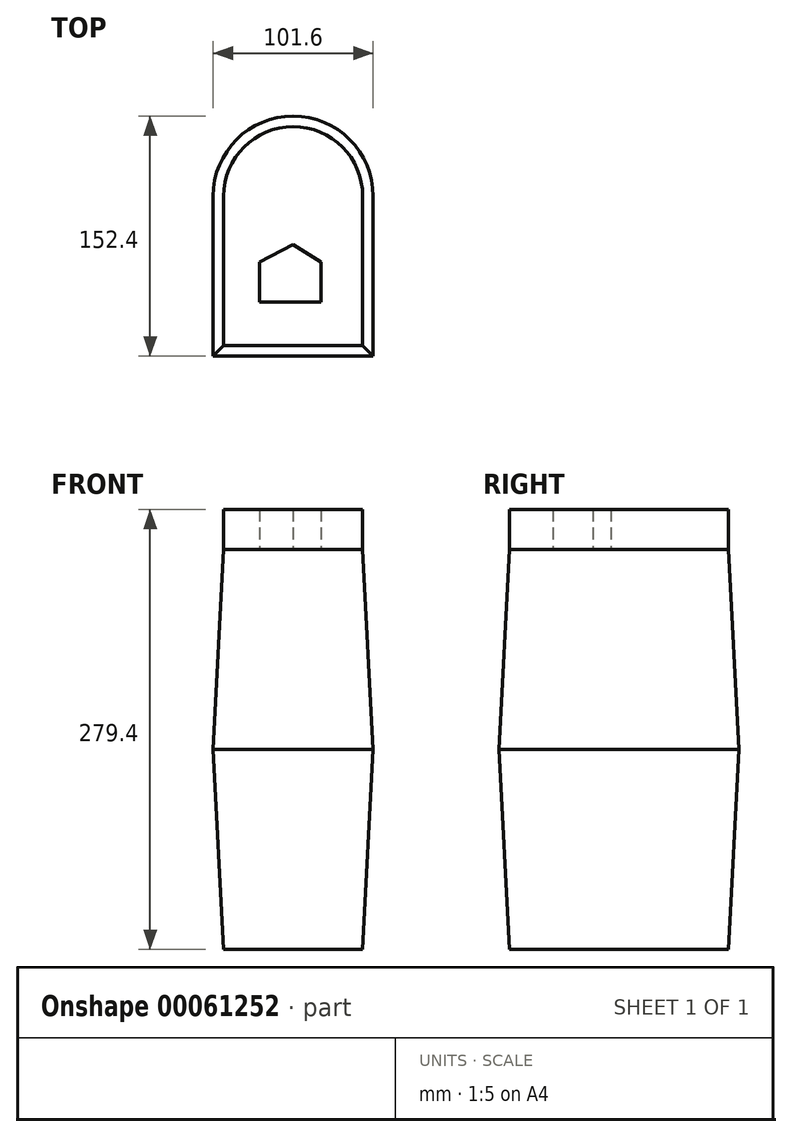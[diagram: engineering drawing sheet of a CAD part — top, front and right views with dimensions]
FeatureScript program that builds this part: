
annotation { "Feature Type Name" : "Feature", "Feature Type Description" : "" }
export const myFeature = defineFeature(function(context is Context, id is Id, definition is map)
    precondition{}
    {
        {
            var Q0;
            Q0=qCreatedBy(makeId("Top.planeOp"),FACE);
            var sketch = newSketch(context, id + "F0", { "sketchPlane" : qUnion([Q0])});
            skLineSegment(sketch, "E0.rect.top", {"start": v(50.8, -50.8) * mm, "end": v(-50.8, -50.8) * mm});
            skLineSegment(sketch, "E0.rect.left", {"start": v(50.8, 50.8) * mm, "end": v(50.8, -50.8) * mm});
            skLineSegment(sketch, "E0.rect.right", {"start": v(-50.8, 50.8) * mm, "end": v(-50.8, -50.8) * mm});
            skPoint(sketch, "E0.rect.middle", {"position": v(0, 0) * mm});
            skArc(sketch, "E1", {"start": v(50.8, 50.8) * mm, "mid": v(0, 101.6) * mm, "end": v(-50.8, 50.8) * mm});
            skSolve(sketch);
        }
        {
            var Q0;
            Q0 = qSketchRegion(id + "F0", true);
            extrude(context, id + "F1", {"entities" : qUnion([Q0]), "endBound" : BoundingType.SYMMETRIC, "depth" : 254 * mm, "hasDraft" : true, "draftAngle" : 3 * degree, "draftPullDirection" : true});
        }
        {
            var Q0;
            Q0=makeQuery(id+"F1.opExtrude","CAP_FACE",FACE,{"disambiguationData":[OSD([sQuery(id+"F0.wireOp",EDGE,"E0.rect.top"),sQuery(id+"F0.wireOp",EDGE,"E0.rect.left"),sQuery(id+"F0.wireOp",EDGE,"E0.rect.right"),sQuery(id+"F0.wireOp",EDGE,"E1")])],"isStart":false});
            var sketch = newSketch(context, id + "F2", { "sketchPlane" : qUnion([Q0])});
            skLineSegment(sketch, "E2.bottom", {"start": v(-21.42, 8.74) * mm, "end": v(17.82, 8.74) * mm});
            skLineSegment(sketch, "E2.top", {"start": v(-21.42, -16.66) * mm, "end": v(17.82, -16.66) * mm});
            skLineSegment(sketch, "E2.left", {"start": v(-21.42, 8.74) * mm, "end": v(-21.42, -16.66) * mm});
            skLineSegment(sketch, "E2.right", {"start": v(17.82, 8.74) * mm, "end": v(17.82, -16.66) * mm});
            skLineSegment(sketch, "E3", {"start": v(-21.42, 8.74) * mm, "end": v(0, 20.1) * mm});
            skLineSegment(sketch, "E4", {"start": v(0, 20.1) * mm, "end": v(17.82, 8.74) * mm});
            skSolve(sketch);
        }
        {
            var Q0;
            Q0=makeQuery(id+"F2.imprint","IMPRINT",FACE,{"disambiguationData":[TD([[makeQuery(id+"F2.imprint","IMPRINT",EDGE,{"derivedFrom":sQuery(id+"F2.wireOp",EDGE,"E2.top")}),-1.0]])]});
            extrude(context, id + "F3", {"entities" : qUnion([Q0]), "operationType" : NewBodyOperationType.ADD, "depth" : 25.4 * mm});
        }
    });
